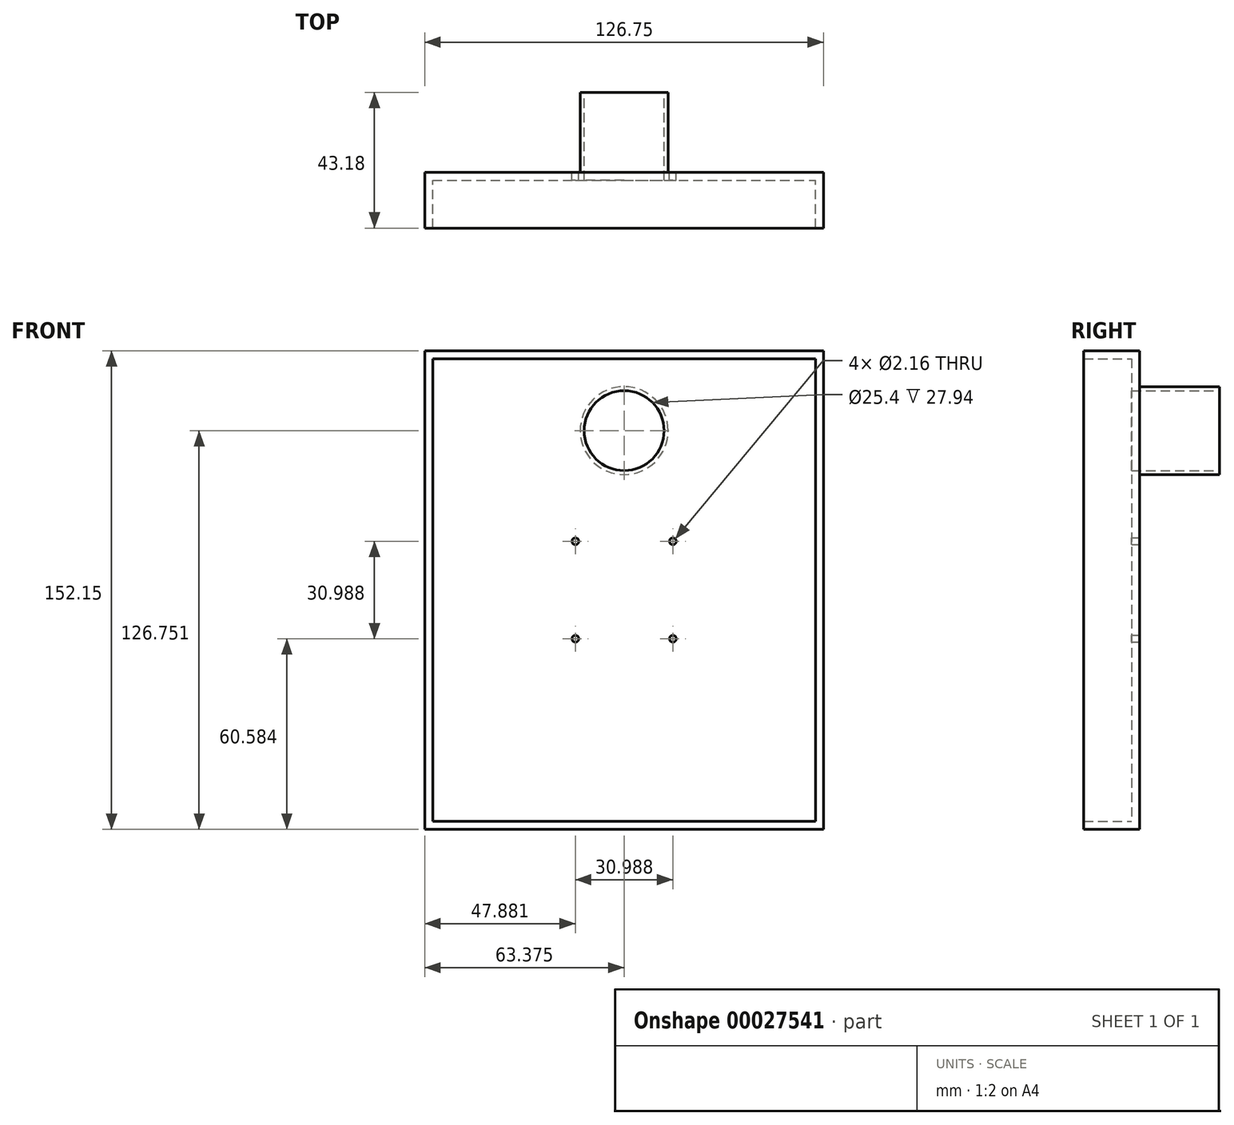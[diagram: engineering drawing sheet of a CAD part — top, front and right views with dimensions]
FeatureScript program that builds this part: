
annotation { "Feature Type Name" : "Feature", "Feature Type Description" : "" }
export const myFeature = defineFeature(function(context is Context, id is Id, definition is map)
    precondition{}
    {
        {
            var Q0;
            Q0=qCreatedBy(makeId("Front.planeOp"),FACE);
            var sketch = newSketch(context, id + "F0", { "sketchPlane" : qUnion([Q0])});
            skLineSegment(sketch, "E0.bottom", {"start": v(-58.06, 109.96) * mm, "end": v(63.6, 109.96) * mm});
            skLineSegment(sketch, "E0.top", {"start": v(-58.06, -37.1) * mm, "end": v(63.6, -37.1) * mm});
            skLineSegment(sketch, "E0.left", {"start": v(-58.06, 109.96) * mm, "end": v(-58.06, -37.1) * mm});
            skLineSegment(sketch, "E0.right", {"start": v(63.6, 109.96) * mm, "end": v(63.6, -37.1) * mm});
            skSolve(sketch);
        }
        {
            var Q0;
            Q0=makeQuery(id+"F0.imprint","IMPRINT",FACE,{"disambiguationData":[TD([[makeQuery(id+"F0.imprint","IMPRINT",EDGE,{"derivedFrom":sQuery(id+"F0.wireOp",EDGE,"E0.bottom")}),-1.0]])]});
            extrude(context, id + "F1", {"entities" : qUnion([Q0]), "depth" : 15.24 * mm});
        }
        {
            var Q0;
            Q0=makeQuery(id+"F1.opExtrude","CAP_FACE",FACE,{"disambiguationData":[OSD([sQuery(id+"F0.wireOp",EDGE,"E0.bottom"),sQuery(id+"F0.wireOp",EDGE,"E0.top"),sQuery(id+"F0.wireOp",EDGE,"E0.left"),sQuery(id+"F0.wireOp",EDGE,"E0.right")])],"isStart":false});
            shell(context, id + "F2", {"entities" : qUnion([Q0]), "thickness" : 2.54 * mm, "oppositeDirection" : true});
        }
        {
            var Q0;
            Q0=makeQuery(id+"F1.opExtrude","CAP_FACE",FACE,{"disambiguationData":[OSD([sQuery(id+"F0.wireOp",EDGE,"E0.bottom"),sQuery(id+"F0.wireOp",EDGE,"E0.top"),sQuery(id+"F0.wireOp",EDGE,"E0.left"),sQuery(id+"F0.wireOp",EDGE,"E0.right")])],"isStart":true});
            var sketch = newSketch(context, id + "F3", { "sketchPlane" : qUnion([Q0])});
            skLineSegment(sketch, "E1", {"start": v(60.6, -39.65) * mm, "end": v(60.6, 20.93) * mm});
            skLineSegment(sketch, "E2", {"start": v(60.6, 20.93) * mm, "end": v(12.72, 20.93) * mm});
            skLineSegment(sketch, "E3", {"start": v(12.72, 20.93) * mm, "end": v(-18.27, 20.93) * mm});
            skLineSegment(sketch, "E4", {"start": v(-18.27, 20.93) * mm, "end": v(-18.27, 51.92) * mm});
            skLineSegment(sketch, "E5", {"start": v(-18.27, 51.92) * mm, "end": v(12.72, 51.92) * mm});
            skCircle(sketch, "E6", {"center": v(12.72, 51.92) * mm, "radius": 1.08 * mm});
            skCircle(sketch, "E7", {"center": v(-18.27, 51.92) * mm, "radius": 1.08 * mm});
            skCircle(sketch, "E8", {"center": v(-18.27, 20.93) * mm, "radius": 1.08 * mm});
            skCircle(sketch, "E9", {"center": v(12.72, 20.93) * mm, "radius": 1.08 * mm});
            skCircle(sketch, "E10", {"center": v(-2.78, 87.1) * mm, "radius": 12.7 * mm});
            skPoint(sketch, "E10.centerSnap0", {"position": v(-2.78, 51.92) * mm});
            skSolve(sketch);
        }
        {
            var Q0;
            Q0=makeQuery(id+"F3.imprint","IMPRINT",FACE,{"disambiguationData":[TD([[makeQuery(id+"F3.imprint","IMPRINT",EDGE,{"derivedFrom":sQuery(id+"F3.wireOp",EDGE,"E6")}),1.0]])]});
            var Q1;
            {var subQ0=sQuery(id+"F3.wireOp",EDGE,"E3");var subQ3=sQuery(id+"F3.wireOp",EDGE,"E2");var subQ4=makeQuery(id+"F3.imprint","INTERSECT",VERTEX,{"derivedFrom":[subQ3,subQ0]});Q1=makeQuery(id+"F3.imprint","IMPRINT",FACE,{"disambiguationData":[TD([[makeQuery(id+"F3.imprint","IMPRINT",EDGE,{"disambiguationData":[TD([[subQ4,1.0]])],"derivedFrom":subQ3}),-1.0]])]});}
            var Q2;
            {var subQ1=sQuery(id+"F3.wireOp",EDGE,"E3");var subQ3=sQuery(id+"F3.wireOp",EDGE,"E2");var subQ5=makeQuery(id+"F3.imprint","INTERSECT",VERTEX,{"derivedFrom":[subQ3,subQ1]});Q2=makeQuery(id+"F3.imprint","IMPRINT",FACE,{"disambiguationData":[TD([[makeQuery(id+"F3.imprint","IMPRINT",EDGE,{"disambiguationData":[TD([[subQ5,1.0]])],"derivedFrom":subQ3}),1.0]])]});}
            var Q3;
            {var subQ0=sQuery(id+"F3.wireOp",EDGE,"E4");var subQ3=sQuery(id+"F3.wireOp",EDGE,"E3");var subQ4=makeQuery(id+"F3.imprint","INTERSECT",VERTEX,{"derivedFrom":[subQ3,subQ0]});Q3=makeQuery(id+"F3.imprint","IMPRINT",FACE,{"disambiguationData":[TD([[makeQuery(id+"F3.imprint","IMPRINT",EDGE,{"disambiguationData":[TD([[subQ4,1.0]])],"derivedFrom":subQ3}),1.0]])]});}
            var Q4;
            {var subQ1=sQuery(id+"F3.wireOp",EDGE,"E4");var subQ3=sQuery(id+"F3.wireOp",EDGE,"E3");var subQ5=makeQuery(id+"F3.imprint","INTERSECT",VERTEX,{"derivedFrom":[subQ3,subQ1]});Q4=makeQuery(id+"F3.imprint","IMPRINT",FACE,{"disambiguationData":[TD([[makeQuery(id+"F3.imprint","IMPRINT",EDGE,{"disambiguationData":[TD([[subQ5,1.0]])],"derivedFrom":subQ3}),-1.0]])]});}
            var Q5;
            {var subQ1=sQuery(id+"F3.wireOp",EDGE,"E5");var subQ3=sQuery(id+"F3.wireOp",EDGE,"E4");var subQ5=makeQuery(id+"F3.imprint","INTERSECT",VERTEX,{"derivedFrom":[subQ3,subQ1]});Q5=makeQuery(id+"F3.imprint","IMPRINT",FACE,{"disambiguationData":[TD([[makeQuery(id+"F3.imprint","IMPRINT",EDGE,{"disambiguationData":[TD([[subQ5,1.0]])],"derivedFrom":subQ3}),1.0]])]});}
            var Q6;
            {var subQ1=sQuery(id+"F3.wireOp",EDGE,"E5");var subQ3=sQuery(id+"F3.wireOp",EDGE,"E4");var subQ5=makeQuery(id+"F3.imprint","INTERSECT",VERTEX,{"derivedFrom":[subQ3,subQ1]});Q6=makeQuery(id+"F3.imprint","IMPRINT",FACE,{"disambiguationData":[TD([[makeQuery(id+"F3.imprint","IMPRINT",EDGE,{"disambiguationData":[TD([[subQ5,1.0]])],"derivedFrom":subQ3}),-1.0]])]});}
            var Q7;
            Q7=makeQuery(id+"F3.imprint","IMPRINT",FACE,{"disambiguationData":[TD([[makeQuery(id+"F3.imprint","IMPRINT",EDGE,{"derivedFrom":sQuery(id+"F3.wireOp",EDGE,"E10")}),1.0]])]});
            extrude(context, id + "F4", {"entities" : qUnion([Q0, Q1, Q2, Q3, Q4, Q5, Q6, Q7]), "operationType" : NewBodyOperationType.REMOVE, "oppositeDirection" : true, "depth" : 20.78 * mm});
        }
        {
            var Q0;
            Q0=makeQuery(id+"F1.opExtrude","CAP_FACE",FACE,{"disambiguationData":[OSD([sQuery(id+"F0.wireOp",EDGE,"E0.bottom"),sQuery(id+"F0.wireOp",EDGE,"E0.top"),sQuery(id+"F0.wireOp",EDGE,"E0.left"),sQuery(id+"F0.wireOp",EDGE,"E0.right")])],"isStart":true});
            var sketch = newSketch(context, id + "F5", { "sketchPlane" : qUnion([Q0])});
            skCircle(sketch, "E11", {"center": v(-2.78, 87.1) * mm, "radius": 13.97 * mm});
            skSolve(sketch);
        }
        {
            var Q0;
            Q0=makeQuery(id+"F5.imprint","IMPRINT",FACE,{"disambiguationData":[TD([[makeQuery(id+"F5.imprint","IMPRINT",EDGE,{"derivedFrom":sQuery(id+"F5.wireOp",EDGE,"E11")}),1.0]])]});
            extrude(context, id + "F6", {"entities" : qUnion([Q0]), "operationType" : NewBodyOperationType.ADD, "depth" : 25.4 * mm});
        }
    });
